# Revit family: FFaucet-Single_Handle-American_Standard-Selectronic_Nextgen-7766.2XX_Series
name_source: partatom
category: Plumbing Fixtures
units: mm (PartAtom-declared; Revit-internal decimal feet)

## family parameters
Always vertical = No
Cut with Voids When Loaded = No
OmniClass Number = 23.45.55.14
OmniClass Title = Single Faucets
Part Type = Normal
Room Calculation Point = No
Round Connector Dimension = Use Diameter
Shared = Yes
Work Plane-Based = Yes

## types (8) — shared parameters
605XRCW Remote control = No
706P400 4" metal deck plate = No
706P800 8" metal deck plate = No
ADA Compliant = Yes
Above Deck Mixing Visibility = Yes
Assembly Code = D2020300
CEC Compliant = Yes
CW Connection = No
CWFU = 1.5
CalGreen Compliant = Yes
Compliance Certifications = These products meet or exceed the following codes and standards: ANSI A117.1, ASME A112.18.1, CSA B 125, NSF 372, NSF 61
Deck Plate Visibility Constraint = No
Default Elevation = 0"
Description = INTEGRATED TOUCHLESS LAVATORY FAUCET WITH ABOVE-DECK MIXING, BATTERY POWERED
Faucet Mounting Height = 0"
HW Connection = No
HWFU = 1.5
Height = 5 3/4"
Installation Type = Deck Mounted
Length = 6 7/8"
Manufacturer = American Standard
Plate Length = 5 1/2"
Plate Width = 2 1/2"
Product Documentation Link = https://lixil.cdn.celum.cloud
Tempered Water Connection = Yes
Tempered Water Connection Diameter = 3/8"
URL = http://www.americanstandard-us.com
Vent Connection = No
WFU = 2
Waste Connection = No
Width = 1 7/8"
Working Pressure = Water pressure range from 20 - 120 psi

## per-type parameters (varying)
| type | Finish | Flow Rate | Flow-Rate | Material |
| 7766203.002 | Metal-American Standard-002-Polished Chrome | 0.35 gpm (1.3 Lpm) | 0 GPM | Metal-American Standard-002-Polished Chrome |
| 7766203.295 | Metal-American Standard-295-Brushed Nickel | 0.35 gpm (1.3 Lpm) | 0 GPM | Metal-American Standard-295-Brushed Nickel |
| 7766205.002 | Metal-American Standard-002-Polished Chrome | 0.5 gpm (1.9 Lpm) | 1 GPM | Metal-American Standard-002-Polished Chrome |
| 7766205.295 | Metal-American Standard-295-Brushed Nickel | 0.5 gpm (1.9 Lpm) | 1 GPM | Metal-American Standard-295-Brushed Nickel |
| 7766215.002 | Metal-American Standard-002-Polished Chrome | 1.5 gpm (5.7 Lpm) | 2 GPM | Metal-American Standard-002-Polished Chrome |
| 7766215.295 | Metal-American Standard-295-Brushed Nickel | 1.5 gpm (5.7 Lpm) | 2 GPM | Metal-American Standard-295-Brushed Nickel |
| 7766205.243 | Metal-American Standard-243-Matte Black | 0.5 gpm (1.9 Lpm) | 1 GPM | Metal-American Standard-243-Matte Black |
| 7766205.GN0 | Metal-American Standard-GN0-Brushed Cool Sunrise | 0.5 gpm (1.9 Lpm) | 1 GPM | Metal-American Standard-GN0-Brushed Cool Sunrise |

note: column(s) folded — value = type name in every type: Model

## geometry (parser evidence)
native form markers: Sweep x4
no freeform markers — native parametric forms only
